# Revit family: Faucet-Single_Control-American_Standard-Delancey_4279410_Series
name_source: partatom
category: Plumbing Fixtures
units: mm (PartAtom-declared; Revit-internal decimal feet)

## family parameters
Always vertical = No
Cut with Voids When Loaded = No
OmniClass Number = 23.45.55.14
OmniClass Title = Single Faucets
Part Type = Normal
Room Calculation Point = No
Round Connector Dimension = Use Diameter
Shared = Yes
Work Plane-Based = Yes

## types (4) — shared parameters
ADA Compliant = Yes
Assembly Code = D2020300
CEC Compliant = Yes
CW Connection = No
CWFU = 1.5
CalGreen Compliant = Yes
Default Elevation = 0"
Description = Delancey® Single-Handle Pull-Down Bar Faucet 1.5 gpm/5.7 L/min
Escutcheon Plate = Yes
Faucet Height Position = 3/8"
Flow Rate = 1.5 gpm (5.7L/min)
HW Connection = No
HWFU = 1.5
Height = 16 11/16"
IAPMO Compliance = Product meets or exceeds: ANSI A117.1, ASME A112.18.1, CSA B125.1, NSF 61/Section 9, NSF 372
Installation Type = Deck Mounted
Length = 10 3/4"
Manufacturer = American Standard
Product Documentation Link = https://americanstandard.box.com
Product Page URL = https://www.americanstandard-us.com
Revised Date = 09/29/2022
Tempered Water Connection = Yes
Tempered Water Connection Diameter = 3/8"
URL = http://www.americanstandard-us.com
Vent Connection = No
WFU = 2
Warranty Information = Limited lifetime warranty on function and finish
Waste Connection = No
Width = 8 11/16"

## per-type parameters (varying)
| type | Finish | Material |
| 4279410.002 | Brass-American Standard-002-Polished Chrome | Brass-American Standard-002-Polished Chrome |
| 4279410.075 | Brass-American Standard-075-Stainless Steel | Brass-American Standard-075-Stainless Steel |
| 4279410.013 | Brass-American Standard-013-Polished Nickel | Brass-American Standard-013-Polished Nickel |
| 4279410.278 | Brass-American Standard-278-Legacy Bronze | Brass-American Standard-278-Legacy Bronze |

note: column(s) folded — value = type name in every type: Model

## geometry (parser evidence)
native form markers: Sweep x6
no freeform markers — native parametric forms only
